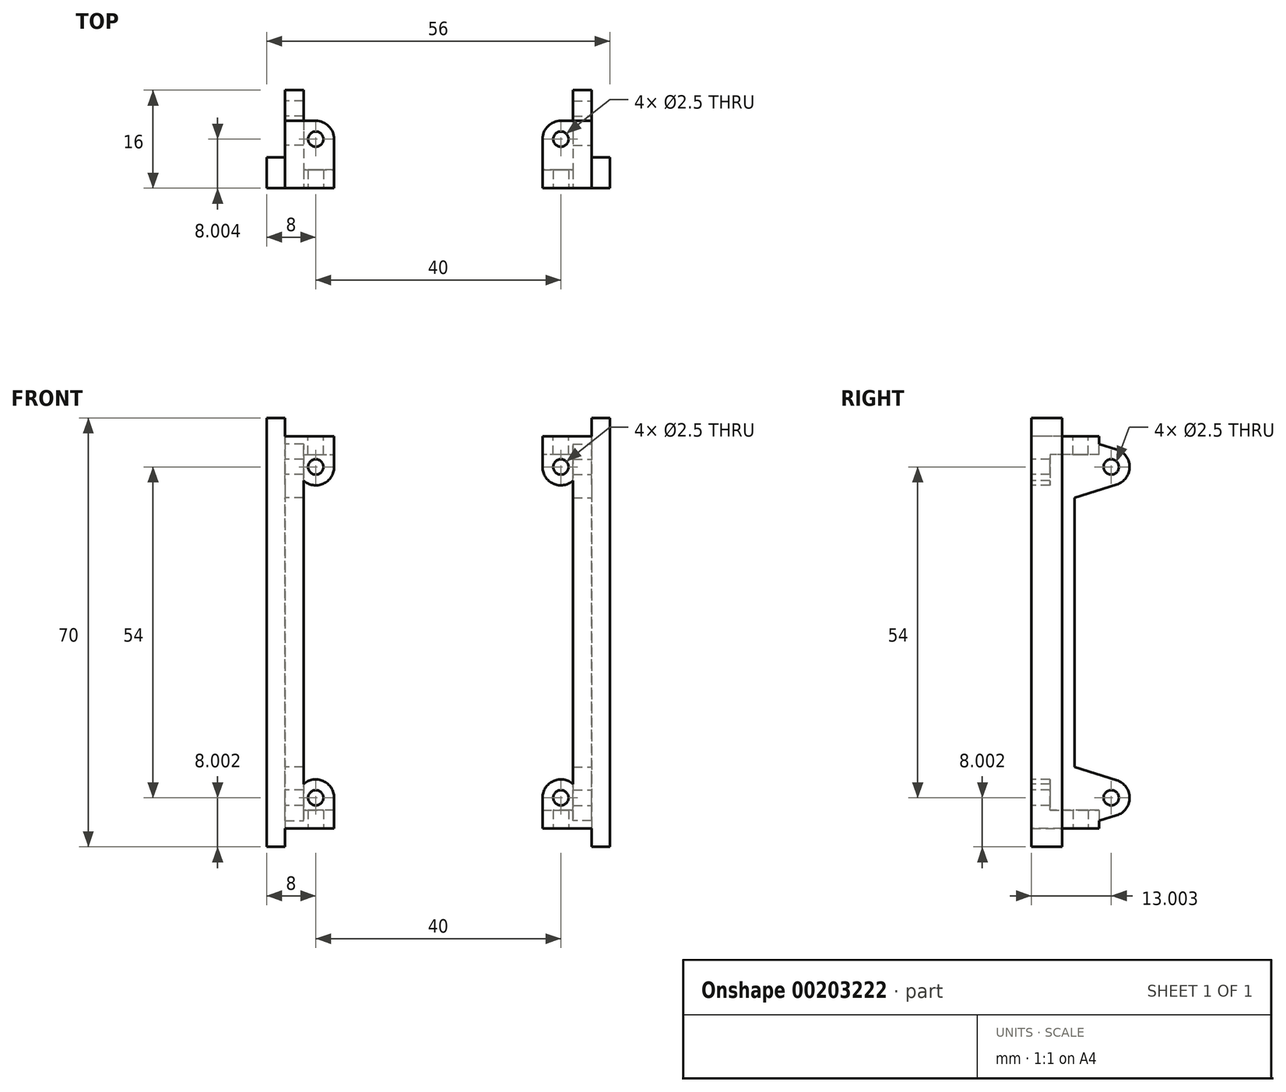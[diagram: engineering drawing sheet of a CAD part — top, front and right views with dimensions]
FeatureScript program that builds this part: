
annotation { "Feature Type Name" : "Feature", "Feature Type Description" : "" }
export const myFeature = defineFeature(function(context is Context, id is Id, definition is map)
    precondition{}
    {
        {
            var Q0;
            Q0=qCreatedBy(makeId("Right.planeOp"),FACE);
            cPlane(context, id + "F0", {"entities" : qUnion([Q0]), "cplaneType" : CPlaneType.OFFSET, "offset" : 25 * mm, "width" : 150 * mm, "height" : 150 * mm});
        }
        {
            var Q0;
            Q0=qCreatedBy(id+"F0.planeOp",FACE);
            var sketch = newSketch(context, id + "F1", { "sketchPlane" : qUnion([Q0])});
            skLineSegment(sketch, "E0.bottom", {"start": v(-0.6, 66.03) * mm, "end": v(4.4, 66.03) * mm});
            skLineSegment(sketch, "E0.top", {"start": v(-0.6, -3.97) * mm, "end": v(4.4, -3.97) * mm});
            skLineSegment(sketch, "E0.left", {"start": v(-0.6, 66.03) * mm, "end": v(-0.6, -3.97) * mm});
            skLineSegment(sketch, "E0.right", {"start": v(4.4, 66.03) * mm, "end": v(4.4, -3.97) * mm});
            skLineSegment(sketch, "E1", {"start": v(4.4, 4.03) * mm, "end": v(12.4, 4.03) * mm, "construction": true});
            skCircle(sketch, "E2", {"center": v(12.4, 4.03) * mm, "radius": 1.25 * mm});
            skLineSegment(sketch, "E3", {"start": v(4.4, 58.03) * mm, "end": v(12.4, 58.03) * mm, "construction": true});
            skCircle(sketch, "E4", {"center": v(12.4, 58.03) * mm, "radius": 1.25 * mm});
            skCircle(sketch, "E5", {"center": v(12.4, 58.03) * mm, "radius": 3 * mm});
            skCircle(sketch, "E6", {"center": v(12.4, 4.03) * mm, "radius": 3 * mm});
            skLineSegment(sketch, "E7", {"start": v(4.4, -0.97) * mm, "end": v(6.4, -0.97) * mm});
            skLineSegment(sketch, "E8", {"start": v(4.4, 63.03) * mm, "end": v(6.4, 63.03) * mm});
            skLineSegment(sketch, "E9", {"start": v(6.4, -0.97) * mm, "end": v(6.4, 63.03) * mm});
            skLineSegment(sketch, "E10", {"start": v(6.4, -0.97) * mm, "end": v(13.3, 1.17) * mm});
            skLineSegment(sketch, "E11", {"start": v(13.3, 6.9) * mm, "end": v(6.4, 9.04) * mm});
            skLineSegment(sketch, "E12", {"start": v(6.4, 63.03) * mm, "end": v(13.3, 60.9) * mm});
            skLineSegment(sketch, "E13", {"start": v(13.3, 55.17) * mm, "end": v(6.4, 53.02) * mm});
            skLineSegment(sketch, "E14", {"start": v(4.4, 63.03) * mm, "end": v(-0.6, 63.03) * mm});
            skLineSegment(sketch, "E15", {"start": v(4.4, -0.97) * mm, "end": v(-0.6, -0.97) * mm});
            skSolve(sketch);
        }
        {
            var Q0;
            {var subQ0=sQuery(id+"F1.wireOp",EDGE,"E0.bottom");Q0=makeQuery(id+"F1.imprint","IMPRINT",FACE,{"disambiguationData":[TD([[makeQuery(id+"F1.imprint","IMPRINT",EDGE,{"derivedFrom":subQ0}),-1.0]])]});}
            var Q1;
            {var subQ0=sQuery(id+"F1.wireOp",EDGE,"E14");Q1=makeQuery(id+"F1.imprint","IMPRINT",FACE,{"disambiguationData":[TD([[makeQuery(id+"F1.imprint","IMPRINT",EDGE,{"derivedFrom":subQ0}),1.0]])]});}
            var Q2;
            {var subQ0=sQuery(id+"F1.wireOp",EDGE,"E0.top");Q2=makeQuery(id+"F1.imprint","IMPRINT",FACE,{"disambiguationData":[TD([[makeQuery(id+"F1.imprint","IMPRINT",EDGE,{"derivedFrom":subQ0}),1.0]])]});}
            extrude(context, id + "F2", {"entities" : qUnion([Q0, Q1, Q2]), "depth" : 3 * mm});
        }
        {
            var Q0;
            Q0=makeQuery(id+"F1.imprint","IMPRINT",FACE,{"disambiguationData":[TD([[makeQuery(id+"F1.imprint","IMPRINT",EDGE,{"derivedFrom":sQuery(id+"F1.wireOp",EDGE,"E2")}),-1.0]])]});
            var Q1;
            Q1=makeQuery(id+"F1.imprint","IMPRINT",FACE,{"disambiguationData":[TD([[makeQuery(id+"F1.imprint","IMPRINT",EDGE,{"derivedFrom":sQuery(id+"F1.wireOp",EDGE,"E4")}),-1.0]])]});
            var Q2;
            {var subQ0=sQuery(id+"F1.wireOp",EDGE,"E12");Q2=makeQuery(id+"F1.imprint","IMPRINT",FACE,{"disambiguationData":[TD([[makeQuery(id+"F1.imprint","IMPRINT",EDGE,{"derivedFrom":subQ0}),-1.0]])]});}
            var Q3;
            {var subQ0=sQuery(id+"F1.wireOp",EDGE,"E10");Q3=makeQuery(id+"F1.imprint","IMPRINT",FACE,{"disambiguationData":[TD([[makeQuery(id+"F1.imprint","IMPRINT",EDGE,{"derivedFrom":subQ0}),1.0]])]});}
            var Q4;
            {var subQ0=sQuery(id+"F1.wireOp",EDGE,"E14");Q4=makeQuery(id+"F1.imprint","IMPRINT",FACE,{"disambiguationData":[TD([[makeQuery(id+"F1.imprint","IMPRINT",EDGE,{"derivedFrom":subQ0}),1.0]])]});}
            var Q5;
            {var subQ1=sQuery(id+"F1.wireOp",EDGE,"E7");Q5=makeQuery(id+"F1.imprint","IMPRINT",FACE,{"disambiguationData":[TD([[makeQuery(id+"F1.imprint","IMPRINT",EDGE,{"derivedFrom":subQ1}),1.0]])]});}
            extrude(context, id + "F3", {"entities" : qUnion([Q0, Q1, Q2, Q3, Q4, Q5]), "operationType" : NewBodyOperationType.ADD, "oppositeDirection" : true, "depth" : 3 * mm});
        }
        {
            var Q0;
            {var subQ0=sQuery(id+"F1.wireOp",EDGE,"E0.left");Q0=makeQuery(id+"F3.boolean.opBoolean","MERGE",FACE,{"derivedFrom":[makeQuery(id+"F2.opExtrude","SWEPT_FACE",FACE,{"disambiguationData":[OSD([subQ0])]}),makeQuery(id+"F3.opExtrude","SWEPT_FACE",FACE,{"disambiguationData":[OSD([subQ0])]})]});}
            var sketch = newSketch(context, id + "F4", { "sketchPlane" : qUnion([Q0])});
            skLineSegment(sketch, "E16", {"start": v(28, 58.03) * mm, "end": v(20, 58.03) * mm, "construction": true});
            skCircle(sketch, "E17", {"center": v(20, 58.03) * mm, "radius": 1.25 * mm});
            skCircle(sketch, "E18", {"center": v(20, 58.03) * mm, "radius": 3 * mm});
            skLineSegment(sketch, "E19", {"start": v(28, 4.03) * mm, "end": v(20, 4.03) * mm, "construction": true});
            skCircle(sketch, "E20", {"center": v(20, 4.03) * mm, "radius": 3 * mm});
            skCircle(sketch, "E21", {"center": v(20, 4.03) * mm, "radius": 1.25 * mm});
            skLineSegment(sketch, "E22", {"start": v(22, 7.03) * mm, "end": v(20, 7.03) * mm});
            skLineSegment(sketch, "E23", {"start": v(22, 55.03) * mm, "end": v(20, 55.03) * mm});
            skLineSegment(sketch, "E24", {"start": v(17, 58.03) * mm, "end": v(17, 61.03) * mm});
            skLineSegment(sketch, "E25", {"start": v(17, 61.03) * mm, "end": v(22, 61.03) * mm});
            skLineSegment(sketch, "E26", {"start": v(22, 1.03) * mm, "end": v(17, 1.03) * mm});
            skLineSegment(sketch, "E27", {"start": v(17, 1.03) * mm, "end": v(17, 4.03) * mm});
            skSolve(sketch);
        }
        {
            var Q0;
            Q0 = qSketchRegion(id + "F4", true);
            extrude(context, id + "F5", {"entities" : qUnion([Q0]), "operationType" : NewBodyOperationType.ADD, "oppositeDirection" : true, "depth" : 3 * mm});
        }
        {
            var Q0;
            Q0=makeQuery(id+"F3.opExtrude","SWEPT_FACE",FACE,{"disambiguationData":[OSD([sQuery(id+"F1.wireOp",EDGE,"E8"),sQuery(id+"F1.wireOp",EDGE,"E14")])]});
            var sketch = newSketch(context, id + "F6", { "sketchPlane" : qUnion([Q0])});
            skLineSegment(sketch, "E28", {"start": v(22, -0.6) * mm, "end": v(20, -0.6) * mm, "construction": true});
            skLineSegment(sketch, "E29", {"start": v(20, -0.6) * mm, "end": v(20, 7.4) * mm, "construction": true});
            skCircle(sketch, "E30", {"center": v(20, 7.4) * mm, "radius": 1.25 * mm});
            skCircle(sketch, "E31", {"center": v(20, 7.4) * mm, "radius": 3 * mm});
            skLineSegment(sketch, "E32", {"start": v(25, 6.4) * mm, "end": v(25, 10.4) * mm});
            skLineSegment(sketch, "E33", {"start": v(25, 10.4) * mm, "end": v(20, 10.4) * mm});
            skLineSegment(sketch, "E34", {"start": v(17, 7.4) * mm, "end": v(17, -0.6) * mm});
            skLineSegment(sketch, "E35", {"start": v(17, -0.6) * mm, "end": v(22, -0.6) * mm});
            skLineSegment(sketch, "E36", {"start": v(22, -0.6) * mm, "end": v(25, -0.6) * mm});
            skLineSegment(sketch, "E37", {"start": v(25, -0.6) * mm, "end": v(25, 6.4) * mm});
            skLineSegment(sketch, "E38", {"start": v(25, 4.4) * mm, "end": v(20, -0.6) * mm});
            skSolve(sketch);
        }
        {
            var Q0;
            Q0 = qSketchRegion(id + "F6", true);
            var Q1;
            {var subQ0=sQuery(id+"F6.wireOp",EDGE,"E34");Q1=makeQuery(id+"F6.imprint","IMPRINT",FACE,{"disambiguationData":[TD([[makeQuery(id+"F6.imprint","IMPRINT",EDGE,{"derivedFrom":subQ0}),1.0]])]});}
            var Q2;
            {var subQ7=sQuery(id+"F6.wireOp",EDGE,"E32");Q2=makeQuery(id+"F6.imprint","IMPRINT",FACE,{"disambiguationData":[TD([[makeQuery(id+"F6.imprint","IMPRINT",EDGE,{"derivedFrom":subQ7}),1.0]])]});}
            extrude(context, id + "F7", {"entities" : qUnion([Q0, Q1, Q2]), "operationType" : NewBodyOperationType.ADD, "oppositeDirection" : true, "depth" : 3 * mm});
        }
        {
            var Q0;
            Q0=makeQuery(id+"F3.opExtrude","SWEPT_FACE",FACE,{"disambiguationData":[OSD([sQuery(id+"F1.wireOp",EDGE,"E7"),sQuery(id+"F1.wireOp",EDGE,"E15")])]});
            var sketch = newSketch(context, id + "F8", { "sketchPlane" : qUnion([Q0])});
            skLineSegment(sketch, "E39", {"start": v(22, 0.6) * mm, "end": v(20, 0.6) * mm, "construction": true});
            skLineSegment(sketch, "E40", {"start": v(20, 0.6) * mm, "end": v(20, -7.4) * mm, "construction": true});
            skCircle(sketch, "E41", {"center": v(20, -7.4) * mm, "radius": 1.25 * mm});
            skCircle(sketch, "E42", {"center": v(20, -7.4) * mm, "radius": 3 * mm});
            skLineSegment(sketch, "E43", {"start": v(25, -6.4) * mm, "end": v(25, -10.4) * mm});
            skLineSegment(sketch, "E44", {"start": v(25, -10.4) * mm, "end": v(20, -10.4) * mm});
            skLineSegment(sketch, "E45", {"start": v(22, 0.6) * mm, "end": v(17, 0.6) * mm});
            skLineSegment(sketch, "E46", {"start": v(17, 0.6) * mm, "end": v(17, -7.4) * mm});
            skSolve(sketch);
        }
        {
            var Q0;
            Q0 = qSketchRegion(id + "F8", true);
            var Q1;
            {var subQ5=sQuery(id+"F8.wireOp",EDGE,"E45");Q1=makeQuery(id+"F8.imprint","IMPRINT",FACE,{"disambiguationData":[TD([[makeQuery(id+"F8.imprint","IMPRINT",EDGE,{"derivedFrom":subQ5}),1.0]])]});}
            var Q2;
            {var subQ7=sQuery(id+"F8.wireOp",EDGE,"E43");Q2=makeQuery(id+"F8.imprint","IMPRINT",FACE,{"disambiguationData":[TD([[makeQuery(id+"F8.imprint","IMPRINT",EDGE,{"derivedFrom":subQ7}),-1.0]])]});}
            extrude(context, id + "F9", {"entities" : qUnion([Q0, Q1, Q2]), "operationType" : NewBodyOperationType.ADD, "oppositeDirection" : true, "depth" : 3 * mm});
        }
        {
            var Q0;
            Q0=makeQuery(id+"F2.opExtrude","SWEPT_BODY",BODY,{"disambiguationData":[OSD([sQuery(id+"F1.wireOp",EDGE,"E0.bottom"),sQuery(id+"F1.wireOp",EDGE,"E0.top"),sQuery(id+"F1.wireOp",EDGE,"E0.left"),sQuery(id+"F1.wireOp",EDGE,"E0.right")])]});
            var Q1;
            Q1=qCreatedBy(makeId("Right.planeOp"),FACE);
            mirror(context, id + "F10", {"entities" : qUnion([Q0]), "mirrorPlane" : qUnion([Q1])});
        }
    });
